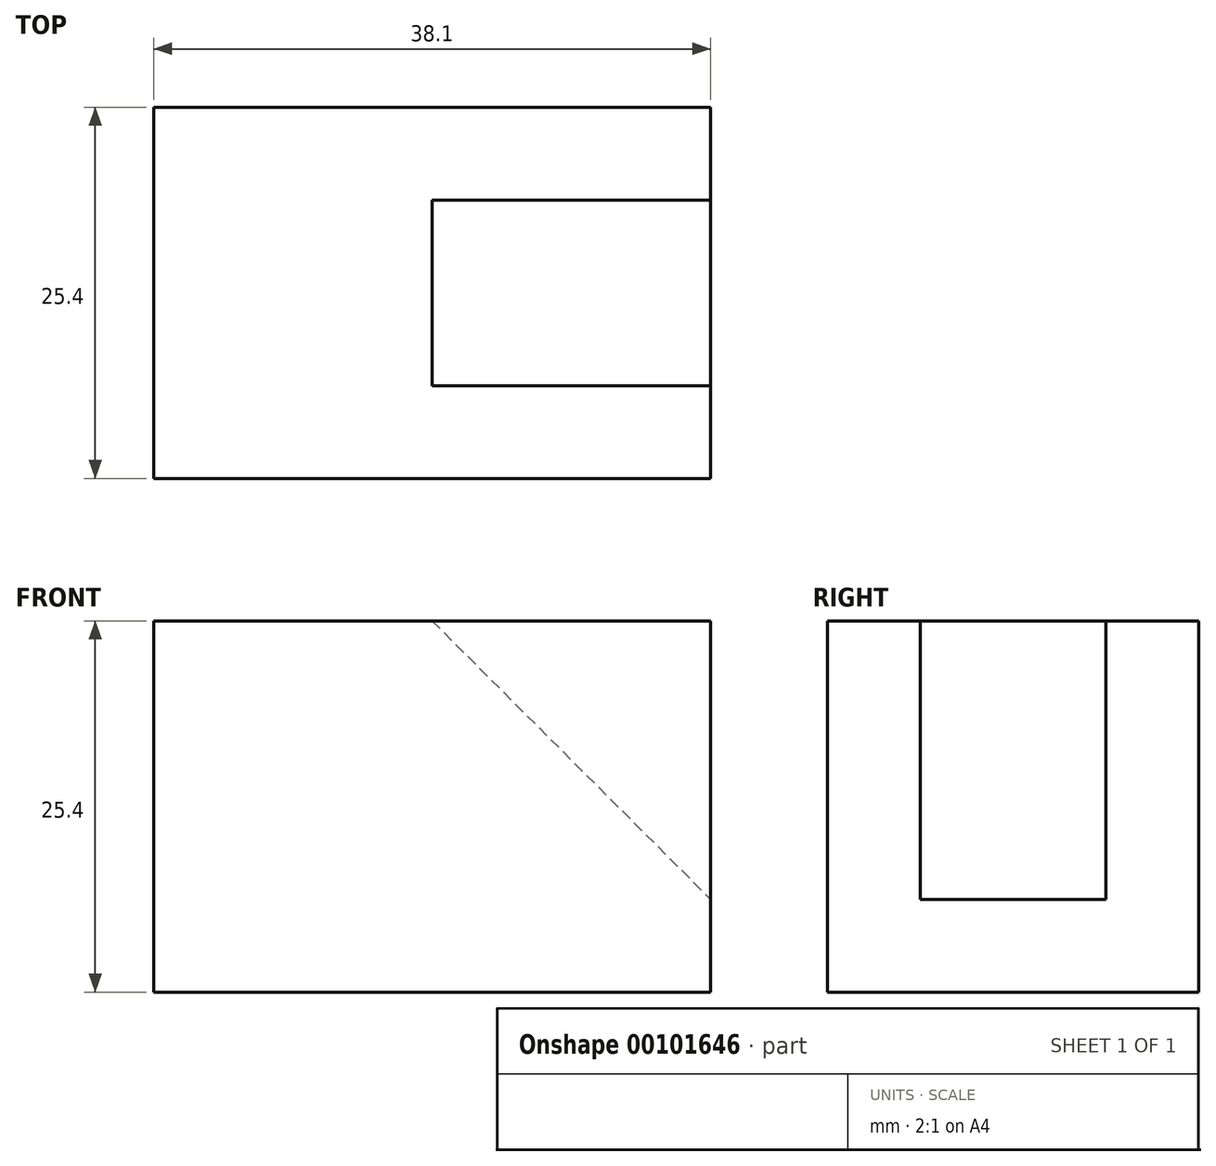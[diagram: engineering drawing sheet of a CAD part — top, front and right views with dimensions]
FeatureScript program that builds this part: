
annotation { "Feature Type Name" : "Feature", "Feature Type Description" : "" }
export const myFeature = defineFeature(function(context is Context, id is Id, definition is map)
    precondition{}
    {
        {
            var Q0;
            Q0=qCreatedBy(makeId("Front.planeOp"),FACE);
            var sketch = newSketch(context, id + "F0", { "sketchPlane" : qUnion([Q0])});
            skLineSegment(sketch, "E0", {"start": v(0, 0) * mm, "end": v(38.1, 0) * mm});
            skLineSegment(sketch, "E1", {"start": v(38.1, 0) * mm, "end": v(38.1, 25.4) * mm});
            skLineSegment(sketch, "E2", {"start": v(38.1, 25.4) * mm, "end": v(0, 25.4) * mm});
            skLineSegment(sketch, "E3", {"start": v(0, 25.4) * mm, "end": v(0, 0) * mm});
            skLineSegment(sketch, "E4", {"start": v(19.05, 25.4) * mm, "end": v(38.1, 6.35) * mm});
            skLineSegment(sketch, "E5", {"start": v(38.1, 6.35) * mm, "end": v(38.1, 25.4) * mm});
            skSolve(sketch);
        }
        {
            var Q0;
            Q0 = qSketchRegion(id + "F0", true);
            extrude(context, id + "F1", {"entities" : qUnion([Q0]), "endBound" : BoundingType.SYMMETRIC, "depth" : 25.4 * mm});
        }
        {
            var Q0;
            {var subQ2=sQuery(id+"F0.wireOp",EDGE,"E4");Q0=makeQuery(id+"F0.imprint","IMPRINT",FACE,{"disambiguationData":[TD([[makeQuery(id+"F0.imprint","IMPRINT",EDGE,{"derivedFrom":subQ2}),1.0]])]});}
            extrude(context, id + "F2", {"entities" : qUnion([Q0]), "operationType" : NewBodyOperationType.REMOVE, "endBound" : BoundingType.SYMMETRIC, "oppositeDirection" : true, "depth" : 12.7 * mm});
        }
    });
